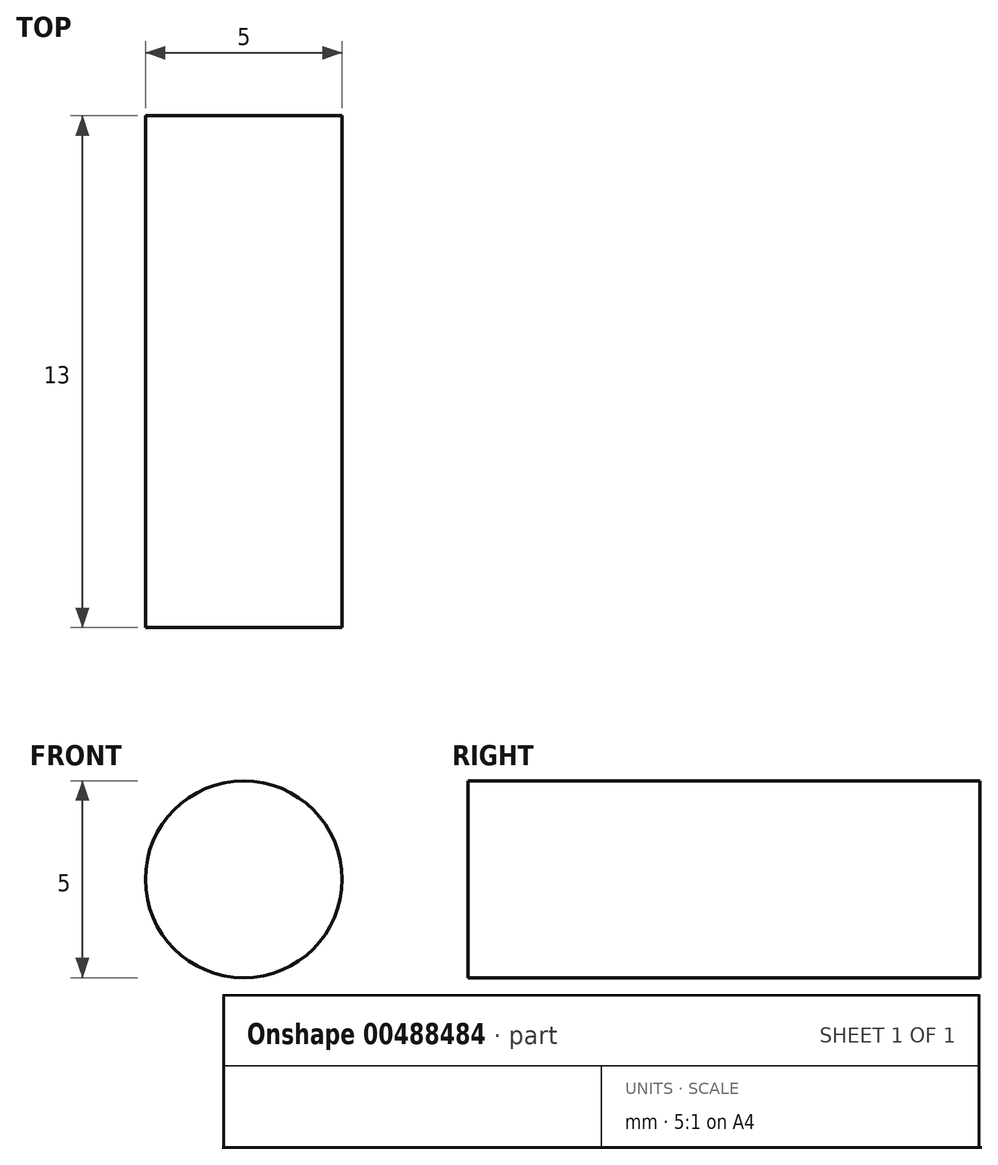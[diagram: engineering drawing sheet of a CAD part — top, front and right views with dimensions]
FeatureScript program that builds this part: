
annotation { "Feature Type Name" : "Feature", "Feature Type Description" : "" }
export const myFeature = defineFeature(function(context is Context, id is Id, definition is map)
    precondition{}
    {
        {
            var Q0;
            Q0=qCreatedBy(makeId("Front.planeOp"),FACE);
            var sketch = newSketch(context, id + "F0", { "sketchPlane" : qUnion([Q0])});
            skCircle(sketch, "E0", {"center": v(0, 0) * mm, "radius": 2.5 * mm});
            skSolve(sketch);
        }
        {
            assignVariable(context, id + "F1", {"name" : "pin_height", "anyValue" : 13});
        }
        {
            var Q0;
            Q0=makeQuery(id+"F0.imprint","IMPRINT",FACE,{"disambiguationData":[TD([[makeQuery(id+"F0.imprint","IMPRINT",EDGE,{"derivedFrom":sQuery(id+"F0.wireOp",EDGE,"E0")}),1.0]])]});
            extrude(context, id + "F2", {"entities" : qUnion([Q0]), "depth" : (getVariable(context, 'pin_height')) * mm});
        }
    });
